# Revit family: TD92_OCA710_BRA010_RVT20_R01
name_source: partatom
category: Mobiliário
units: mm (PartAtom-declared; Revit-internal decimal feet)

## family parameters
Com base no plano de trabalho = Não
Compartilhado = Não
Corte com vazios quando carregada = Não
Número OmniClass = 23.40.20.00
Ponto de cálculo do ambiente = Não
Sempre na vertical = Sim
Título OmniClass = General Furniture and Specialties

## types (1)
- TD92_OCA710_BRA010_RVT20_R01
    Descrição = Forma pura, conforto pleno e alegria no ambiente. O real sentido da palavra oca serviu de inspiração para o desenvolvimento da Poltrona Tramontina Oca em Polietileno, que acomoda com total conforto e decora o ambiente com uma nova proposta visual. Disponível em diversas cores, ela torna o ambiente mais tranquilo e harmonioso. Criada com o conceito de durabilidade, garantimos um produto que você poderá ter por muitos anos em sua casa.
    Elevação padrão = 0  [stored 0 ft]
    Fabricante = Tramontina Delta S.A
    Modelo = Poltrona Tramontina Oca em Polietileno Branco
    Nota-chave = 92710010
    URL = https://www.tramontinastore.com

note: [stored X ft] marks values corroborated as IEEE doubles in the binary element streams (Revit-internal decimal feet)
